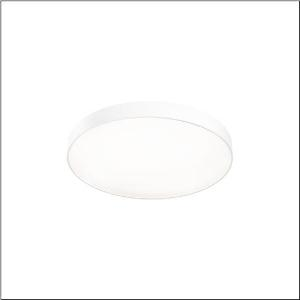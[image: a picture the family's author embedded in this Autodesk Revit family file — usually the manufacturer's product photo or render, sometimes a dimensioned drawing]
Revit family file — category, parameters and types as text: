
# Revit family: round_21_m_51mr36gd0421w
name_source: partatom
category: Lighting Fixtures
units: mm (PartAtom-declared; Revit-internal decimal feet)

## family parameters
Cut with Voids When Loaded = No
Host = Face
Light Source = No
Part Type = Normal
Room Calculation Point = No
Round Connector Dimension = Use Diameter
Shared = No

## types (1)
- Round 21 M (1 x LED, 7160 lm, 54.5 W, 4000K)
    Apparent Load = 55 VA
    CIE Flux Codes = 49 80 96 85 100
    Color Rendering = 80
    Color Temperature = 4000K
    Default Elevation = 1800 mm
    Description = Round 21 M, wall and ceiling luminaire, primary optical cover: cover, of PMMA, opal, light emission: direct/indirect distribution, primary light characteristic: symmetric, installation type: suspended mounting, surface-mounted, LED, rated luminous flux: 7.110lm, luminous efficacy: 130lm/W, light colour: 840, colour temperature: 4000K, with terminal, 5-pole, mains connection: 230V, AC, 50/60Hz, rated input power: 55W, housing, of aluminium, coated, white, diameter: 600mm, height: 62mm, protection rating (complete): IP40, insulation class (complete): insulation class I (protective earthing), certification: CE, impact resistance: IK04, permissible operating ambient temperature: -10..+35°C, packaging unit: 1 piece
    Height = 87 mm
    Lamp = 1 x LED
    Lamp Light Flux = 7160 lm
    Lamp Power = 54.5 W
    Lamp count = 1
    Length = 600 mm
    Luminous efficacy = 131 lm/W
    Manufacturer = Siteco
    ModVariant = No
    Model = 51MR36GD0421W
    Mounting Place = Ceiling
    Mounting Type = Surface mounted
    Number of Poles = 1
    OnlyDefault = Yes
    Power Factor = 1
    Product Name = Round 21 M
    Product group = wall and ceiling luminaire
    ProductGroupID = 302
    Protection Class = Protection class I
    Protection Degree = IP 40
    RLX_Detail_Level = 1
    RLX_Emergency_Light_Flux = 0 lm
    RLX_Emergency_Type = 0
    RLX_Emergency_Type_DB = No
    RlxData = <blob elided: 12081 chars, md5=8aabab65>
    Socket = socket
    Standby Power = 0 W
    System Light Flux = 7160 lm
    System Power = 55 W
    Type Comments = Product without accessories
    Type Image = l_1258330.jpg
    URL = http://relux.com
    VarID = ---
    Voltage = 0 V
    Weight = 0.00 kg
    Width = 0 mm  [stored 0 ft]

note: [stored X ft] marks values corroborated as IEEE doubles in the binary element streams (Revit-internal decimal feet)

## geometry (parser evidence)
native form markers: Sweep x12
no freeform markers — native parametric forms only
